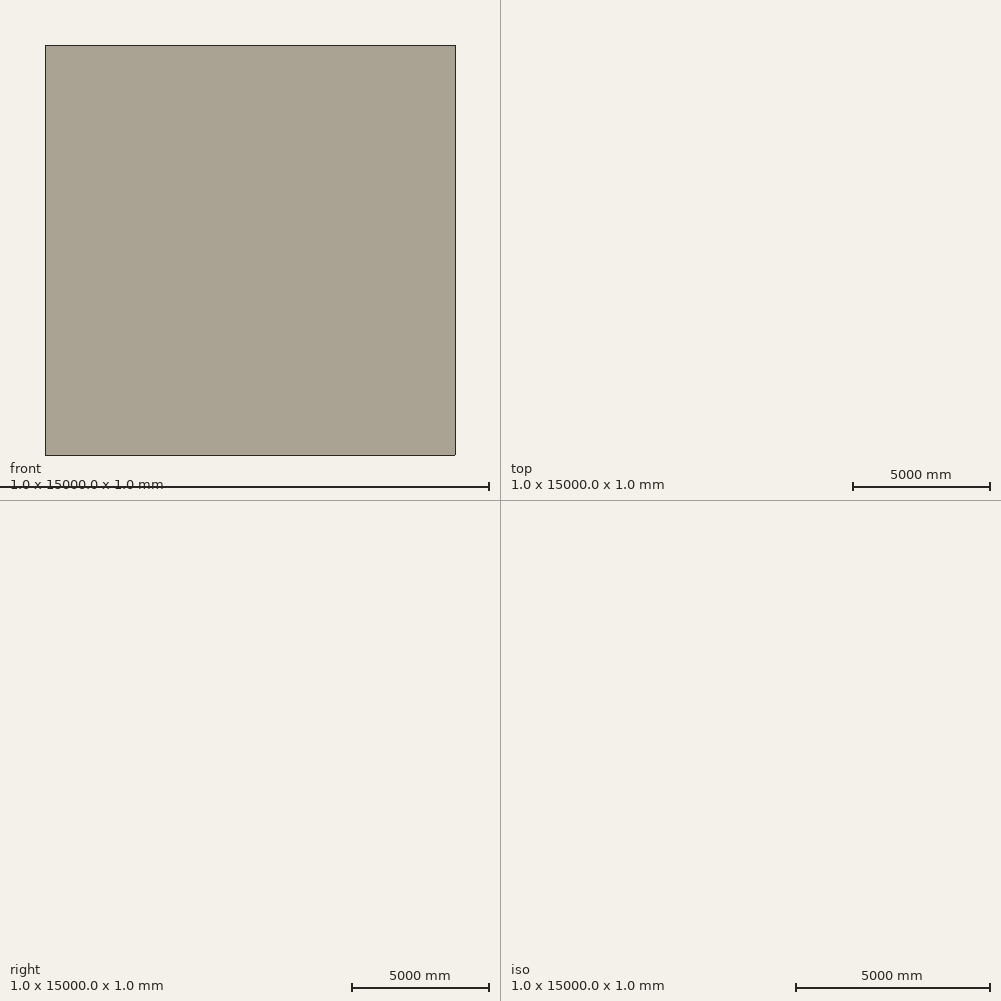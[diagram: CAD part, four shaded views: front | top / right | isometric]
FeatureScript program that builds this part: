
annotation { "Feature Type Name" : "Feature", "Feature Type Description" : "" }
export const myFeature = defineFeature(function(context is Context, id is Id, definition is map)
    precondition{}
    {
        {
            var Q0;
            Q0=qCreatedBy(makeId("Front.planeOp"),FACE);
            var sketch = newSketch(context, id + "F0", { "sketchPlane" : qUnion([Q0])});
            skLineSegment(sketch, "E0.bottom", {"start": v(0.5, -0.5) * mm, "end": v(-0.5, -0.5) * mm});
            skLineSegment(sketch, "E0.top", {"start": v(0.5, 0.5) * mm, "end": v(-0.5, 0.5) * mm});
            skLineSegment(sketch, "E0.left", {"start": v(0.5, -0.5) * mm, "end": v(0.5, 0.5) * mm});
            skLineSegment(sketch, "E0.right", {"start": v(-0.5, -0.5) * mm, "end": v(-0.5, 0.5) * mm});
            skPoint(sketch, "E0.middle", {"position": v(0, 0) * mm});
            skSolve(sketch);
        }
        {
            var Q0;
            Q0=makeQuery(id+"F0.imprint","IMPRINT",FACE,{"disambiguationData":[TD([[makeQuery(id+"F0.imprint","IMPRINT",EDGE,{"derivedFrom":sQuery(id+"F0.wireOp",EDGE,"E0.bottom")}),-1.0]])]});
            extrude(context, id + "F1", {"entities" : qUnion([Q0]), "depth" : 15000 * mm, "offsetDistance" : 25 * mm});
        }
    });
